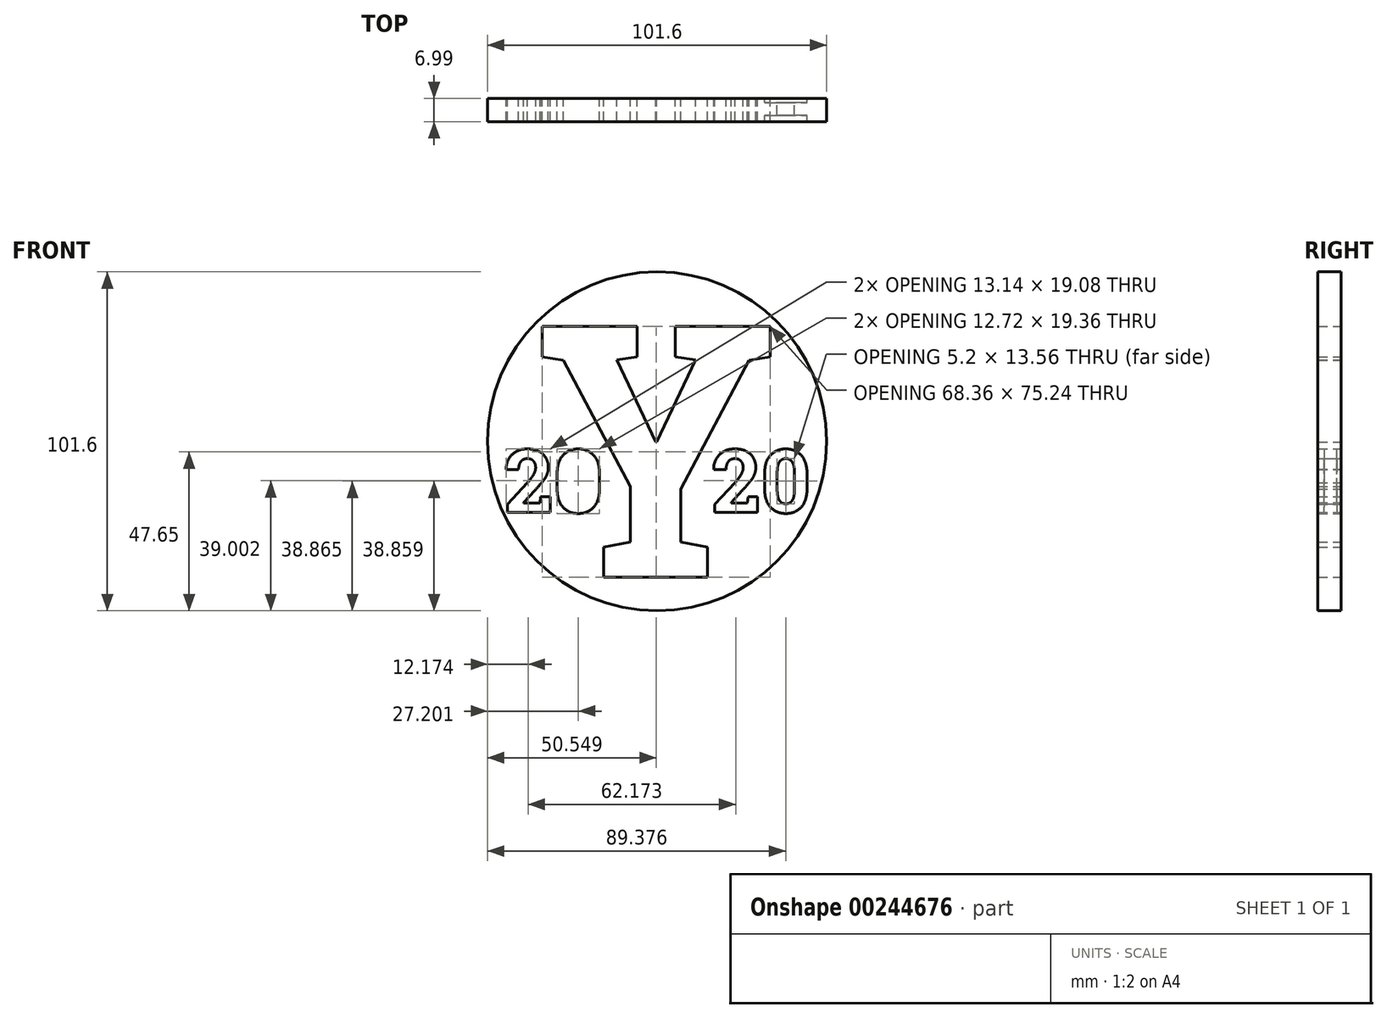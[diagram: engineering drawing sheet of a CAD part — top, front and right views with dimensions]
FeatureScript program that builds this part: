
annotation { "Feature Type Name" : "Feature", "Feature Type Description" : "" }
export const myFeature = defineFeature(function(context is Context, id is Id, definition is map)
    precondition{}
    {
        {
            var Q0;
            Q0=qCreatedBy(makeId("Front.planeOp"),FACE);
            var sketch = newSketch(context, id + "F0", { "sketchPlane" : qUnion([Q0])});
            skCircle(sketch, "E0", {"center": v(0, 0) * mm, "radius": 50.8 * mm});
            skText(sketch, "E1", { "text": "Y", "fontName": "RobotoSlab-Bold.ttf"});
            skText(sketch, "E2", { "text": "20     20", "fontName": "RobotoSlab-Bold.ttf"});
            const initialGuessF0  = {"E1": [-0.0363, -0.04077, 1, 0, 0.0762], "E2": [-0.04584, -0.02134, 1, 0, 0.01905]};
            skSetInitialGuess(sketch, initialGuessF0);
            skSolve(sketch);
        }
        {
            var Q0;
            Q0=makeQuery(id+"F0.imprint","IMPRINT",FACE,{"disambiguationData":[TD([[makeQuery(id+"F0.imprint","IMPRINT",EDGE,{"derivedFrom":sQuery(id+"F0.wireOp",EDGE,"E2.sketch_text.stroke-66")}),-1.0]])]});
            extrude(context, id + "F1", {"entities" : qUnion([Q0]), "endBound" : BoundingType.SYMMETRIC, "depth" : 3.8 * mm});
        }
        {
            var Q0;
            Q0 = qSketchRegion(id + "F0", true);
            extrude(context, id + "F2", {"entities" : qUnion([Q0]), "operationType" : NewBodyOperationType.ADD, "endBound" : BoundingType.SYMMETRIC, "depth" : 6.35 * mm});
        }
        {
            var Q0;
            Q0 = qSketchRegion(id + "F0", true);
            extrude(context, id + "F3", {"entities" : qUnion([Q0]), "operationType" : NewBodyOperationType.ADD, "depth" : 3.8 * mm});
        }
    });
